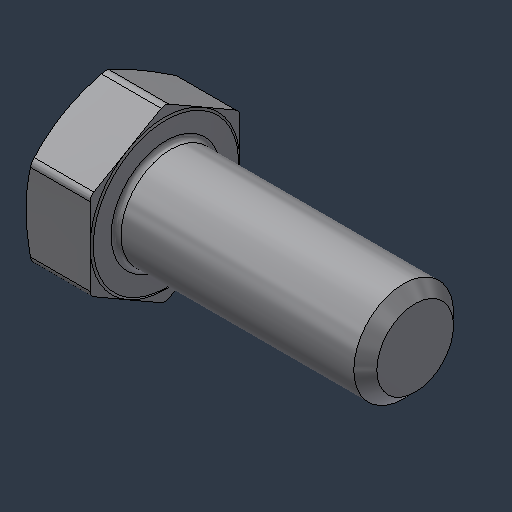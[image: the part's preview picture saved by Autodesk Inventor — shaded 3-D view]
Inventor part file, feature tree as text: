
AUTODESK INVENTOR PART (.ipt)
format: ipt  version: 2024.3 (Build 283343000, 343)  size: 176,128 bytes
history: native  units: mm (DEFAULTED — no unit token found)
features: fillet x1
ambient origin geometry x8: Origin, YZ Plane, XZ Plane, XY Plane, X Axis, Y Axis, Z Axis, Center Point
bodies: Solid1 (feature_tree)
feature tree (1):
  fillet  "Fillet4"  [1 undecoded]
note: 1 required parameter value undecoded (feature->parameter linkage not recoverable at this tier; creation-order binding heuristic only, values carry confidence <= 0.55)
